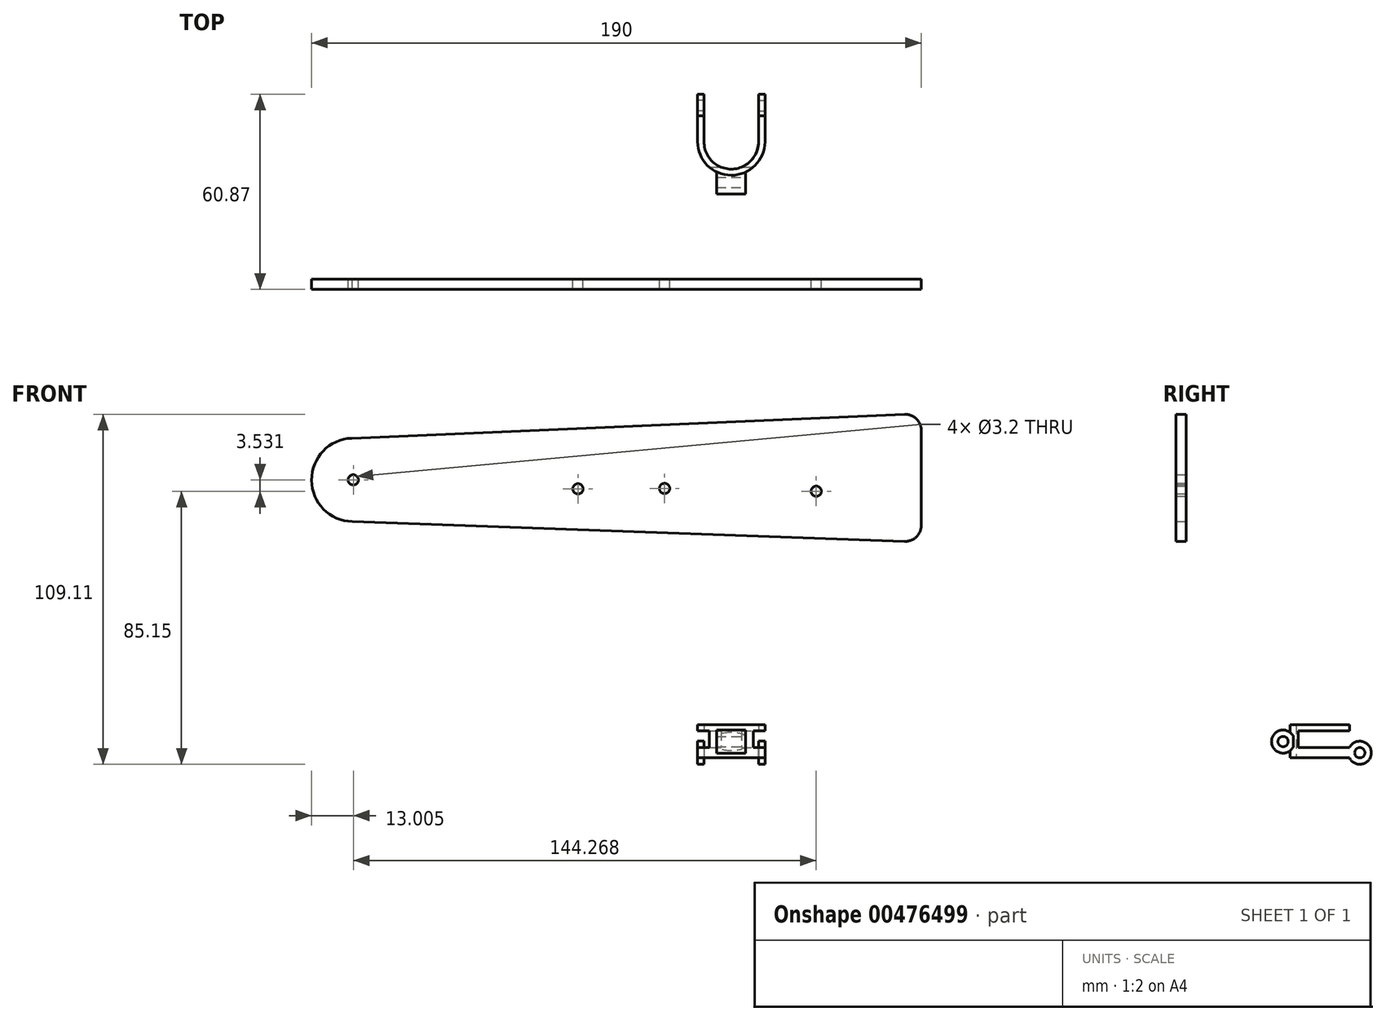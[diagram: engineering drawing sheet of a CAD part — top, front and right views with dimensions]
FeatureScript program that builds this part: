
annotation { "Feature Type Name" : "Feature", "Feature Type Description" : "" }
export const myFeature = defineFeature(function(context is Context, id is Id, definition is map)
    precondition{}
    {
        {
            var Q0;
            Q0=qCreatedBy(makeId("Front.planeOp"),FACE);
            var sketch = newSketch(context, id + "F0", { "sketchPlane" : qUnion([Q0])});
            skLineSegment(sketch, "E0", {"start": v(59.2, 102.1) * mm, "end": v(59.2, 72.51) * mm});
            skLineSegment(sketch, "E1", {"start": v(54, 107.1) * mm, "end": v(-118.27, 99.68) * mm});
            skLineSegment(sketch, "E2", {"start": v(54.03, 67.52) * mm, "end": v(-118.1, 73.68) * mm});
            skArc(sketch, "E3", {"start": v(-118.27, 99.68) * mm, "mid": v(-130.8, 86.6) * mm, "end": v(-118.1, 73.68) * mm});
            skCircle(sketch, "E4", {"center": v(-117.79, 86.68) * mm, "radius": 1.6 * mm});
            skCircle(sketch, "E5", {"center": v(26.48, 83.15) * mm, "radius": 1.6 * mm});
            skPoint(sketch, "E6.visualSharp", {"position": v(59.2, 107.33) * mm});
            skArc(sketch, "E6.filletArc", {"start": v(59.2, 102.1) * mm, "mid": v(57.67, 105.72) * mm, "end": v(54, 107.1) * mm});
            skPoint(sketch, "E7.visualSharp", {"position": v(59.2, 67.33) * mm});
            skArc(sketch, "E7.filletArc", {"start": v(54.03, 67.52) * mm, "mid": v(57.68, 68.91) * mm, "end": v(59.2, 72.51) * mm});
            skCircle(sketch, "E8", {"center": v(-47.79, 83.89) * mm, "radius": 1.6 * mm});
            skCircle(sketch, "E9", {"center": v(-20.8, 84) * mm, "radius": 1.6 * mm});
            skSolve(sketch);
        }
        {
            var Q0;
            Q0=makeQuery(id+"F0.imprint","IMPRINT",FACE,{"disambiguationData":[TD([[makeQuery(id+"F0.imprint","IMPRINT",EDGE,{"derivedFrom":sQuery(id+"F0.wireOp",EDGE,"E0")}),-1.0]])]});
            extrude(context, id + "F1", {"entities" : qUnion([Q0]), "depth" : 3.2 * mm, "offsetDistance" : 25 * mm});
        }
        {
            var Q0;
            Q0=qCreatedBy(makeId("Top.planeOp"),FACE);
            var sketch = newSketch(context, id + "F2", { "sketchPlane" : qUnion([Q0])});
            skPoint(sketch, "E10.middle", {"position": v(0, 42.47) * mm});
            skCircle(sketch, "E11", {"center": v(0, 42.47) * mm, "radius": 8.5 * mm, "construction": true});
            skCircle(sketch, "E12", {"center": v(0, 42.47) * mm, "radius": 10.1 * mm, "construction": true});
            skLineSegment(sketch, "E13.bottom", {"start": v(-8.5, 42.85) * mm, "end": v(-10.5, 42.85) * mm});
            skLineSegment(sketch, "E13.top", {"start": v(-8.5, 50.85) * mm, "end": v(-10.5, 50.85) * mm});
            skLineSegment(sketch, "E13.left", {"start": v(-8.5, 42.85) * mm, "end": v(-8.5, 50.85) * mm});
            skLineSegment(sketch, "E13.right", {"start": v(-10.5, 42.85) * mm, "end": v(-10.5, 50.85) * mm});
            skLineSegment(sketch, "E14.bottom", {"start": v(8.49, 42.78) * mm, "end": v(10.49, 42.78) * mm});
            skLineSegment(sketch, "E14.top", {"start": v(8.49, 50.85) * mm, "end": v(10.49, 50.85) * mm});
            skLineSegment(sketch, "E14.left", {"start": v(8.49, 42.78) * mm, "end": v(8.49, 50.85) * mm});
            skLineSegment(sketch, "E14.right", {"start": v(10.49, 42.78) * mm, "end": v(10.49, 50.85) * mm});
            skArc(sketch, "E15", {"start": v(-10.5, 42.85) * mm, "mid": v(-0.04, 32.36) * mm, "end": v(10.49, 42.78) * mm});
            skArc(sketch, "E16", {"start": v(8.49, 42.78) * mm, "mid": v(-0.04, 34.3) * mm, "end": v(-8.5, 42.85) * mm});
            skSolve(sketch);
        }
        {
            var Q0;
            Q0=makeQuery(id+"F2.imprint","IMPRINT",FACE,{"disambiguationData":[TD([[makeQuery(id+"F2.imprint","IMPRINT",EDGE,{"derivedFrom":sQuery(id+"F2.wireOp",EDGE,"E13.bottom")}),-1.0]])]});
            var Q1;
            Q1=makeQuery(id+"F2.imprint","IMPRINT",FACE,{"disambiguationData":[TD([[makeQuery(id+"F2.imprint","IMPRINT",EDGE,{"derivedFrom":sQuery(id+"F2.wireOp",EDGE,"E13.bottom")}),1.0]])]});
            var Q2;
            Q2=makeQuery(id+"F2.imprint","IMPRINT",FACE,{"disambiguationData":[TD([[makeQuery(id+"F2.imprint","IMPRINT",EDGE,{"derivedFrom":sQuery(id+"F2.wireOp",EDGE,"E14.bottom")}),1.0]])]});
            extrude(context, id + "F3", {"entities" : qUnion([Q0, Q1, Q2]), "depth" : 3.2 * mm, "offsetDistance" : 25 * mm});
        }
        {
            var Q0;
            Q0=makeQuery(id+"F3.opExtrude","SWEPT_FACE",FACE,{"disambiguationData":[OSD([sQuery(id+"F2.wireOp",EDGE,"E13.right")])]});
            var sketch = newSketch(context, id + "F4", { "sketchPlane" : qUnion([Q0])});
            skPoint(sketch, "E17", {"position": v(-50.85, 0) * mm});
            skPoint(sketch, "E18", {"position": v(-50.85, 3.2) * mm});
            skArc(sketch, "E19", {"start": v(-50.85, 3.2) * mm, "mid": v(-57.67, 1.6) * mm, "end": v(-50.85, 0) * mm});
            skCircle(sketch, "E20", {"center": v(-54.07, 1.6) * mm, "radius": 1.6 * mm});
            skSolve(sketch);
        }
        {
            var Q0;
            Q0=makeQuery(id+"F4.imprint","IMPRINT",FACE,{"disambiguationData":[TD([[makeQuery(id+"F4.imprint","IMPRINT",EDGE,{"derivedFrom":sQuery(id+"F4.wireOp",EDGE,"E19")}),1.0]])]});
            extrude(context, id + "F5", {"entities" : qUnion([Q0]), "operationType" : NewBodyOperationType.ADD, "oppositeDirection" : true, "depth" : 2 * mm, "offsetDistance" : 25 * mm});
        }
        {
            var Q0;
            Q0=makeQuery(id+"F3.opExtrude","SWEPT_FACE",FACE,{"disambiguationData":[OSD([sQuery(id+"F2.wireOp",EDGE,"E14.right")])]});
            var sketch = newSketch(context, id + "F6", { "sketchPlane" : qUnion([Q0])});
            skPoint(sketch, "E21", {"position": v(50.85, 3.2) * mm});
            skPoint(sketch, "E22", {"position": v(50.85, 0) * mm});
            skArc(sketch, "E23", {"start": v(50.85, 0) * mm, "mid": v(57.67, 1.6) * mm, "end": v(50.85, 3.2) * mm});
            skCircle(sketch, "E24", {"center": v(54.07, 1.6) * mm, "radius": 1.6 * mm});
            skSolve(sketch);
        }
        {
            var Q0;
            Q0=makeQuery(id+"F6.imprint","IMPRINT",FACE,{"disambiguationData":[TD([[makeQuery(id+"F6.imprint","IMPRINT",EDGE,{"derivedFrom":sQuery(id+"F6.wireOp",EDGE,"E23")}),1.0]])]});
            extrude(context, id + "F7", {"entities" : qUnion([Q0]), "operationType" : NewBodyOperationType.ADD, "oppositeDirection" : true, "depth" : 2 * mm, "offsetDistance" : 25 * mm});
        }
        {
            var Q0;
            {var subQ0=sQuery(id+"F2.wireOp",EDGE,"E14.right");Q0=makeQuery(id+"F7.boolean.opBoolean","MERGE",FACE,{"derivedFrom":[makeQuery(id+"F3.opExtrude","SWEPT_FACE",FACE,{"disambiguationData":[OSD([subQ0])]}),makeQuery(id+"F7.opExtrude","CAP_FACE",FACE,{"disambiguationData":[OSD([sQuery(id+"F2.wireOp",EDGE,"E14.top"),subQ0,sQuery(id+"F6.wireOp",EDGE,"E23"),sQuery(id+"F6.wireOp",EDGE,"E24")])],"isStart":true})]});}
            var sketch = newSketch(context, id + "F8", { "sketchPlane" : qUnion([Q0])});
            skPoint(sketch, "E25", {"position": v(33.4, 3.5) * mm});
            skPoint(sketch, "E26", {"position": v(33.39, 6.7) * mm});
            skArc(sketch, "E27", {"start": v(33.39, 6.7) * mm, "mid": v(26.57, 5.07) * mm, "end": v(33.4, 3.5) * mm});
            skCircle(sketch, "E28", {"center": v(30.17, 5.08) * mm, "radius": 1.6 * mm});
            skLineSegment(sketch, "E29", {"start": v(33.4, 3.5) * mm, "end": v(33.39, 6.7) * mm});
            skSolve(sketch);
        }
        {
            var Q0;
            Q0=makeQuery(id+"F8.imprint","IMPRINT",FACE,{"disambiguationData":[TD([[makeQuery(id+"F8.imprint","IMPRINT",EDGE,{"derivedFrom":sQuery(id+"F8.wireOp",EDGE,"E27")}),1.0]])]});
            extrude(context, id + "F9", {"entities" : qUnion([Q0]), "operationType" : NewBodyOperationType.ADD, "oppositeDirection" : true, "depth" : 15.1 * mm, "offsetDistance" : 25 * mm, "hasSecondDirection" : true, "secondDirectionOppositeDirection" : true, "secondDirectionDepth" : 6 * mm});
        }
        {
            var Q0;
            Q0=makeQuery(id+"F2.imprint","IMPRINT",FACE,{"disambiguationData":[TD([[makeQuery(id+"F2.imprint","IMPRINT",EDGE,{"derivedFrom":sQuery(id+"F2.wireOp",EDGE,"E13.bottom")}),1.0]])]});
            extrude(context, id + "F10", {"entities" : qUnion([Q0]), "operationType" : NewBodyOperationType.ADD, "depth" : 10.4 * mm, "offsetDistance" : 25 * mm});
        }
        {
            var Q0;
            {var subQ0=sQuery(id+"F2.wireOp",EDGE,"E16");var subQ1=sQuery(id+"F2.wireOp",EDGE,"E15");var subQ4=sQuery(id+"F2.wireOp",EDGE,"E14.right");var subQ5=sQuery(id+"F2.wireOp",EDGE,"E14.top");var subQ6=sQuery(id+"F2.wireOp",EDGE,"E14.left");Q0=makeQuery(id+"F10.boolean.opBoolean","SPLIT",FACE,{"disambiguationData":[TD([makeQuery(id+"F3.opExtrude","SWEPT_FACE",FACE,{"disambiguationData":[OSD([subQ6])]})])],"derivedFrom":makeQuery(id+"F3.opExtrude","CAP_FACE",FACE,{"disambiguationData":[OSD([sQuery(id+"F2.wireOp",EDGE,"E13.top"),sQuery(id+"F2.wireOp",EDGE,"E13.left"),sQuery(id+"F2.wireOp",EDGE,"E13.right"),subQ5,subQ6,subQ4,subQ1,subQ0])],"isStart":false})});}
            var Q1;
            {var subQ0=sQuery(id+"F2.wireOp",EDGE,"E16");var subQ1=sQuery(id+"F2.wireOp",EDGE,"E13.right");var subQ2=sQuery(id+"F2.wireOp",EDGE,"E15");var subQ3=sQuery(id+"F2.wireOp",EDGE,"E13.left");var subQ6=sQuery(id+"F2.wireOp",EDGE,"E13.top");Q1=makeQuery(id+"F10.boolean.opBoolean","SPLIT",FACE,{"disambiguationData":[TD([makeQuery(id+"F3.opExtrude","SWEPT_FACE",FACE,{"disambiguationData":[OSD([subQ3])]})])],"derivedFrom":makeQuery(id+"F3.opExtrude","CAP_FACE",FACE,{"disambiguationData":[OSD([subQ6,subQ3,subQ1,sQuery(id+"F2.wireOp",EDGE,"E14.top"),sQuery(id+"F2.wireOp",EDGE,"E14.left"),sQuery(id+"F2.wireOp",EDGE,"E14.right"),subQ2,subQ0])],"isStart":false})});}
            extrude(context, id + "F11", {"entities" : qUnion([Q0, Q1]), "operationType" : NewBodyOperationType.ADD, "depth" : 7.2 * mm, "offsetDistance" : 25 * mm, "hasSecondDirection" : true, "secondDirectionOppositeDirection" : false, "secondDirectionDepth" : 5.2 * mm});
        }
        {
            var Q0;
            {var subQ0=sQuery(id+"F2.wireOp",EDGE,"E14.right");Q0=makeQuery(id+"F7.boolean.opBoolean","MERGE",FACE,{"derivedFrom":[makeQuery(id+"F3.opExtrude","SWEPT_FACE",FACE,{"disambiguationData":[OSD([subQ0])]}),makeQuery(id+"F7.opExtrude","CAP_FACE",FACE,{"disambiguationData":[OSD([sQuery(id+"F2.wireOp",EDGE,"E14.top"),subQ0,sQuery(id+"F6.wireOp",EDGE,"E23"),sQuery(id+"F6.wireOp",EDGE,"E24")])],"isStart":true})]});}
            var sketch = newSketch(context, id + "F12", { "sketchPlane" : qUnion([Q0])});
            skPoint(sketch, "E30", {"position": v(42.91, 8.4) * mm});
            skPoint(sketch, "E31", {"position": v(42.91, 3.2) * mm});
            skLineSegment(sketch, "E32.bottom", {"start": v(42.91, 8.4) * mm, "end": v(34.91, 8.4) * mm});
            skLineSegment(sketch, "E32.top", {"start": v(42.91, 3.2) * mm, "end": v(34.91, 3.2) * mm});
            skLineSegment(sketch, "E32.left", {"start": v(42.91, 8.4) * mm, "end": v(42.91, 3.2) * mm});
            skLineSegment(sketch, "E32.right", {"start": v(34.91, 8.4) * mm, "end": v(34.91, 3.2) * mm});
            skSolve(sketch);
        }
        {
            var Q0;
            Q0 = qSketchRegion(id + "F12", true);
            extrude(context, id + "F13", {"entities" : qUnion([Q0]), "operationType" : NewBodyOperationType.REMOVE, "endBound" : BoundingType.THROUGH_ALL, "oppositeDirection" : true, "depth" : 25 * mm, "offsetDistance" : 25 * mm});
        }
    });
